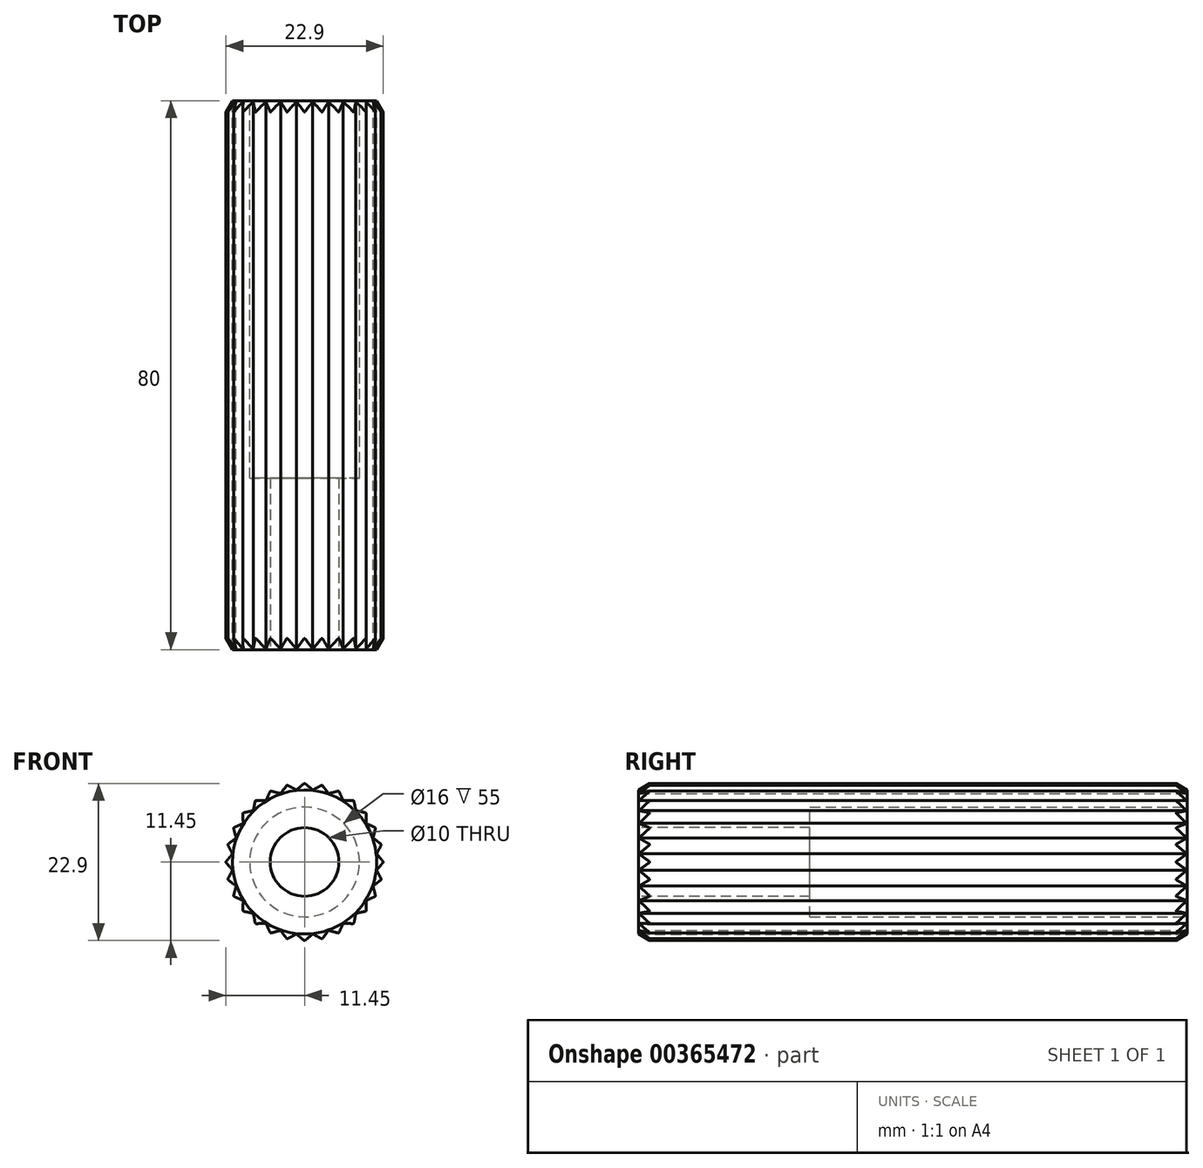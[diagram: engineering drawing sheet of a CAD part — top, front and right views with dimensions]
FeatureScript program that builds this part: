
annotation { "Feature Type Name" : "Feature", "Feature Type Description" : "" }
export const myFeature = defineFeature(function(context is Context, id is Id, definition is map)
    precondition{}
    {
        {
            var Q0;
            Q0=qCreatedBy(makeId("Front.planeOp"),FACE);
            var sketch = newSketch(context, id + "F0", { "sketchPlane" : qUnion([Q0])});
            skCircle(sketch, "E0", {"center": v(0, 0) * mm, "radius": 8 * mm});
            skLineSegment(sketch, "E1", {"start": v(0, 0) * mm, "end": v(0, 8) * mm});
            skLineSegment(sketch, "E2", {"start": v(-0.12, 11.4) * mm, "end": v(-1.73, 10.05) * mm});
            skLineSegment(sketch, "E3.MirrorCS", {"start": v(0.12, 11.4) * mm, "end": v(1.73, 10.05) * mm});
            skPoint(sketch, "E4.visualSharp", {"position": v(0, 11.5) * mm});
            skArc(sketch, "E4.filletArc", {"start": v(0.12, 11.4) * mm, "mid": v(0, 11.45) * mm, "end": v(-0.12, 11.4) * mm});
            skLineSegment(sketch, "E5.1.0", {"start": v(-2.65, 11.1) * mm, "end": v(-3.92, 9.42) * mm});
            skLineSegment(sketch, "E5.1.1", {"start": v(-2.42, 11.14) * mm, "end": v(-0.55, 10.18) * mm});
            skArc(sketch, "E5.1.2", {"start": v(-2.42, 11.14) * mm, "mid": v(-2.55, 11.16) * mm, "end": v(-2.65, 11.1) * mm});
            skLineSegment(sketch, "E5.2.0", {"start": v(-5.05, 10.22) * mm, "end": v(-5.92, 8.3) * mm});
            skLineSegment(sketch, "E5.2.1", {"start": v(-4.84, 10.32) * mm, "end": v(-2.8, 9.8) * mm});
            skArc(sketch, "E5.2.2", {"start": v(-4.84, 10.32) * mm, "mid": v(-4.97, 10.31) * mm, "end": v(-5.05, 10.22) * mm});
            skLineSegment(sketch, "E5.3.0", {"start": v(-7.2, 8.84) * mm, "end": v(-7.62, 6.78) * mm});
            skLineSegment(sketch, "E5.3.1", {"start": v(-7.02, 8.99) * mm, "end": v(-4.92, 8.93) * mm});
            skArc(sketch, "E5.3.2", {"start": v(-7.02, 8.99) * mm, "mid": v(-7.14, 8.95) * mm, "end": v(-7.2, 8.84) * mm});
            skLineSegment(sketch, "E5.4.0", {"start": v(-8.99, 7.02) * mm, "end": v(-8.93, 4.92) * mm});
            skLineSegment(sketch, "E5.4.1", {"start": v(-8.84, 7.2) * mm, "end": v(-6.78, 7.62) * mm});
            skArc(sketch, "E5.4.2", {"start": v(-8.84, 7.2) * mm, "mid": v(-8.95, 7.14) * mm, "end": v(-8.99, 7.02) * mm});
            skLineSegment(sketch, "E5.5.0", {"start": v(-10.32, 4.84) * mm, "end": v(-9.8, 2.8) * mm});
            skLineSegment(sketch, "E5.5.1", {"start": v(-10.22, 5.05) * mm, "end": v(-8.3, 5.92) * mm});
            skArc(sketch, "E5.5.2", {"start": v(-10.22, 5.05) * mm, "mid": v(-10.31, 4.97) * mm, "end": v(-10.32, 4.84) * mm});
            skLineSegment(sketch, "E5.6.0", {"start": v(-11.14, 2.42) * mm, "end": v(-10.18, 0.55) * mm});
            skLineSegment(sketch, "E5.6.1", {"start": v(-11.1, 2.65) * mm, "end": v(-9.42, 3.92) * mm});
            skArc(sketch, "E5.6.2", {"start": v(-11.1, 2.65) * mm, "mid": v(-11.16, 2.55) * mm, "end": v(-11.14, 2.42) * mm});
            skLineSegment(sketch, "E5.7.0", {"start": v(-11.4, -0.12) * mm, "end": v(-10.05, -1.73) * mm});
            skLineSegment(sketch, "E5.7.1", {"start": v(-11.4, 0.12) * mm, "end": v(-10.05, 1.73) * mm});
            skArc(sketch, "E5.7.2", {"start": v(-11.4, 0.12) * mm, "mid": v(-11.45, 0) * mm, "end": v(-11.4, -0.12) * mm});
            skLineSegment(sketch, "E5.8.0", {"start": v(-11.1, -2.65) * mm, "end": v(-9.42, -3.92) * mm});
            skLineSegment(sketch, "E5.8.1", {"start": v(-11.14, -2.42) * mm, "end": v(-10.18, -0.55) * mm});
            skArc(sketch, "E5.8.2", {"start": v(-11.14, -2.42) * mm, "mid": v(-11.16, -2.55) * mm, "end": v(-11.1, -2.65) * mm});
            skLineSegment(sketch, "E5.9.0", {"start": v(-10.22, -5.05) * mm, "end": v(-8.3, -5.92) * mm});
            skLineSegment(sketch, "E5.9.1", {"start": v(-10.32, -4.84) * mm, "end": v(-9.8, -2.8) * mm});
            skArc(sketch, "E5.9.2", {"start": v(-10.32, -4.84) * mm, "mid": v(-10.31, -4.97) * mm, "end": v(-10.22, -5.05) * mm});
            skLineSegment(sketch, "E5.10.0", {"start": v(-8.84, -7.2) * mm, "end": v(-6.78, -7.62) * mm});
            skLineSegment(sketch, "E5.10.1", {"start": v(-8.99, -7.02) * mm, "end": v(-8.93, -4.92) * mm});
            skArc(sketch, "E5.10.2", {"start": v(-8.99, -7.02) * mm, "mid": v(-8.95, -7.14) * mm, "end": v(-8.84, -7.2) * mm});
            skLineSegment(sketch, "E5.11.0", {"start": v(-7.02, -8.99) * mm, "end": v(-4.92, -8.93) * mm});
            skLineSegment(sketch, "E5.11.1", {"start": v(-7.2, -8.84) * mm, "end": v(-7.62, -6.78) * mm});
            skArc(sketch, "E5.11.2", {"start": v(-7.2, -8.84) * mm, "mid": v(-7.14, -8.95) * mm, "end": v(-7.02, -8.99) * mm});
            skLineSegment(sketch, "E5.12.0", {"start": v(-4.84, -10.32) * mm, "end": v(-2.8, -9.8) * mm});
            skLineSegment(sketch, "E5.12.1", {"start": v(-5.05, -10.22) * mm, "end": v(-5.92, -8.3) * mm});
            skArc(sketch, "E5.12.2", {"start": v(-5.05, -10.22) * mm, "mid": v(-4.97, -10.31) * mm, "end": v(-4.84, -10.32) * mm});
            skLineSegment(sketch, "E5.13.0", {"start": v(-2.42, -11.14) * mm, "end": v(-0.55, -10.18) * mm});
            skLineSegment(sketch, "E5.13.1", {"start": v(-2.65, -11.1) * mm, "end": v(-3.92, -9.42) * mm});
            skArc(sketch, "E5.13.2", {"start": v(-2.65, -11.1) * mm, "mid": v(-2.55, -11.16) * mm, "end": v(-2.42, -11.14) * mm});
            skLineSegment(sketch, "E5.14.0", {"start": v(0.12, -11.4) * mm, "end": v(1.73, -10.05) * mm});
            skLineSegment(sketch, "E5.14.1", {"start": v(-0.12, -11.4) * mm, "end": v(-1.73, -10.05) * mm});
            skArc(sketch, "E5.14.2", {"start": v(-0.12, -11.4) * mm, "mid": v(0, -11.45) * mm, "end": v(0.12, -11.4) * mm});
            skLineSegment(sketch, "E5.15.0", {"start": v(2.65, -11.1) * mm, "end": v(3.92, -9.42) * mm});
            skLineSegment(sketch, "E5.15.1", {"start": v(2.42, -11.14) * mm, "end": v(0.55, -10.18) * mm});
            skArc(sketch, "E5.15.2", {"start": v(2.42, -11.14) * mm, "mid": v(2.55, -11.16) * mm, "end": v(2.65, -11.1) * mm});
            skLineSegment(sketch, "E5.16.0", {"start": v(5.05, -10.22) * mm, "end": v(5.92, -8.3) * mm});
            skLineSegment(sketch, "E5.16.1", {"start": v(4.84, -10.32) * mm, "end": v(2.8, -9.8) * mm});
            skArc(sketch, "E5.16.2", {"start": v(4.84, -10.32) * mm, "mid": v(4.97, -10.31) * mm, "end": v(5.05, -10.22) * mm});
            skLineSegment(sketch, "E5.17.0", {"start": v(7.2, -8.84) * mm, "end": v(7.62, -6.78) * mm});
            skLineSegment(sketch, "E5.17.1", {"start": v(7.02, -8.99) * mm, "end": v(4.92, -8.93) * mm});
            skArc(sketch, "E5.17.2", {"start": v(7.02, -8.99) * mm, "mid": v(7.14, -8.95) * mm, "end": v(7.2, -8.84) * mm});
            skLineSegment(sketch, "E5.18.0", {"start": v(8.99, -7.02) * mm, "end": v(8.93, -4.92) * mm});
            skLineSegment(sketch, "E5.18.1", {"start": v(8.84, -7.2) * mm, "end": v(6.78, -7.62) * mm});
            skArc(sketch, "E5.18.2", {"start": v(8.84, -7.2) * mm, "mid": v(8.95, -7.14) * mm, "end": v(8.99, -7.02) * mm});
            skLineSegment(sketch, "E5.19.0", {"start": v(10.32, -4.84) * mm, "end": v(9.8, -2.8) * mm});
            skLineSegment(sketch, "E5.19.1", {"start": v(10.22, -5.05) * mm, "end": v(8.3, -5.92) * mm});
            skArc(sketch, "E5.19.2", {"start": v(10.22, -5.05) * mm, "mid": v(10.31, -4.97) * mm, "end": v(10.32, -4.84) * mm});
            skLineSegment(sketch, "E5.20.0", {"start": v(11.14, -2.42) * mm, "end": v(10.18, -0.55) * mm});
            skLineSegment(sketch, "E5.20.1", {"start": v(11.1, -2.65) * mm, "end": v(9.42, -3.92) * mm});
            skArc(sketch, "E5.20.2", {"start": v(11.1, -2.65) * mm, "mid": v(11.16, -2.55) * mm, "end": v(11.14, -2.42) * mm});
            skLineSegment(sketch, "E5.21.0", {"start": v(11.4, 0.12) * mm, "end": v(10.05, 1.73) * mm});
            skLineSegment(sketch, "E5.21.1", {"start": v(11.4, -0.12) * mm, "end": v(10.05, -1.73) * mm});
            skArc(sketch, "E5.21.2", {"start": v(11.4, -0.12) * mm, "mid": v(11.45, 0) * mm, "end": v(11.4, 0.12) * mm});
            skLineSegment(sketch, "E5.22.0", {"start": v(11.1, 2.65) * mm, "end": v(9.42, 3.92) * mm});
            skLineSegment(sketch, "E5.22.1", {"start": v(11.14, 2.42) * mm, "end": v(10.18, 0.55) * mm});
            skArc(sketch, "E5.22.2", {"start": v(11.14, 2.42) * mm, "mid": v(11.16, 2.55) * mm, "end": v(11.1, 2.65) * mm});
            skLineSegment(sketch, "E5.23.0", {"start": v(10.22, 5.05) * mm, "end": v(8.3, 5.92) * mm});
            skLineSegment(sketch, "E5.23.1", {"start": v(10.32, 4.84) * mm, "end": v(9.8, 2.8) * mm});
            skArc(sketch, "E5.23.2", {"start": v(10.32, 4.84) * mm, "mid": v(10.31, 4.97) * mm, "end": v(10.22, 5.05) * mm});
            skLineSegment(sketch, "E5.24.0", {"start": v(8.84, 7.2) * mm, "end": v(6.78, 7.62) * mm});
            skLineSegment(sketch, "E5.24.1", {"start": v(8.99, 7.02) * mm, "end": v(8.93, 4.92) * mm});
            skArc(sketch, "E5.24.2", {"start": v(8.99, 7.02) * mm, "mid": v(8.95, 7.14) * mm, "end": v(8.84, 7.2) * mm});
            skLineSegment(sketch, "E5.25.0", {"start": v(7.02, 8.99) * mm, "end": v(4.92, 8.93) * mm});
            skLineSegment(sketch, "E5.25.1", {"start": v(7.2, 8.84) * mm, "end": v(7.62, 6.78) * mm});
            skArc(sketch, "E5.25.2", {"start": v(7.2, 8.84) * mm, "mid": v(7.14, 8.95) * mm, "end": v(7.02, 8.99) * mm});
            skLineSegment(sketch, "E5.26.0", {"start": v(4.84, 10.32) * mm, "end": v(2.8, 9.8) * mm});
            skLineSegment(sketch, "E5.26.1", {"start": v(5.05, 10.22) * mm, "end": v(5.92, 8.3) * mm});
            skArc(sketch, "E5.26.2", {"start": v(5.05, 10.22) * mm, "mid": v(4.97, 10.31) * mm, "end": v(4.84, 10.32) * mm});
            skLineSegment(sketch, "E5.27.0", {"start": v(2.42, 11.14) * mm, "end": v(0.55, 10.18) * mm});
            skLineSegment(sketch, "E5.27.1", {"start": v(2.65, 11.1) * mm, "end": v(3.92, 9.42) * mm});
            skArc(sketch, "E5.27.2", {"start": v(2.65, 11.1) * mm, "mid": v(2.55, 11.16) * mm, "end": v(2.42, 11.14) * mm});
            skSolve(sketch);
        }
        {
            var Q0;
            Q0 = qSketchRegion(id + "F0", true);
            extrude(context, id + "F1", {"entities" : qUnion([Q0]), "depth" : 80 * mm});
        }
        {
            var Q0;
            Q0=makeQuery(id+"F1.opExtrude","CAP_FACE",FACE,{"disambiguationData":[OSD([sQuery(id+"F0.wireOp",EDGE,"lSqxqfwO-eqKo-ZCZg-UigB-sFxWdEm8U8hB"),sQuery(id+"F0.wireOp",EDGE,"E0"),sQuery(id+"F0.wireOp",EDGE,"C1UlFKiI-6M3d-ekVj-oFgV-l0cv2vAE1tmQ"),sQuery(id+"F0.wireOp",EDGE,"baf2f13f-041f-44b5-8537-4fbedda5209f0.MirrorCS"),sQuery(id+"F0.wireOp",EDGE,"b2c0e1ce-1615-419f-ab4c-fed52ce990dc.filletArc"),sQuery(id+"F0.wireOp",EDGE,"31b1d020-76b6-4874-875a-db2137b606a0.1.0"),sQuery(id+"F0.wireOp",EDGE,"31b1d020-76b6-4874-875a-db2137b606a0.1.1"),sQuery(id+"F0.wireOp",EDGE,"31b1d020-76b6-4874-875a-db2137b606a0.1.2"),sQuery(id+"F0.wireOp",EDGE,"31b1d020-76b6-4874-875a-db2137b606a0.2.0"),sQuery(id+"F0.wireOp",EDGE,"31b1d020-76b6-4874-875a-db2137b606a0.2.1"),sQuery(id+"F0.wireOp",EDGE,"31b1d020-76b6-4874-875a-db2137b606a0.2.2"),sQuery(id+"F0.wireOp",EDGE,"31b1d020-76b6-4874-875a-db2137b606a0.3.0"),sQuery(id+"F0.wireOp",EDGE,"31b1d020-76b6-4874-875a-db2137b606a0.3.1"),sQuery(id+"F0.wireOp",EDGE,"31b1d020-76b6-4874-875a-db2137b606a0.3.2"),sQuery(id+"F0.wireOp",EDGE,"31b1d020-76b6-4874-875a-db2137b606a0.4.0"),sQuery(id+"F0.wireOp",EDGE,"31b1d020-76b6-4874-875a-db2137b606a0.4.1"),sQuery(id+"F0.wireOp",EDGE,"31b1d020-76b6-4874-875a-db2137b606a0.4.2"),sQuery(id+"F0.wireOp",EDGE,"31b1d020-76b6-4874-875a-db2137b606a0.5.0"),sQuery(id+"F0.wireOp",EDGE,"31b1d020-76b6-4874-875a-db2137b606a0.5.1"),sQuery(id+"F0.wireOp",EDGE,"31b1d020-76b6-4874-875a-db2137b606a0.5.2"),sQuery(id+"F0.wireOp",EDGE,"31b1d020-76b6-4874-875a-db2137b606a0.6.0"),sQuery(id+"F0.wireOp",EDGE,"31b1d020-76b6-4874-875a-db2137b606a0.6.1"),sQuery(id+"F0.wireOp",EDGE,"31b1d020-76b6-4874-875a-db2137b606a0.6.2"),sQuery(id+"F0.wireOp",EDGE,"31b1d020-76b6-4874-875a-db2137b606a0.7.0"),sQuery(id+"F0.wireOp",EDGE,"31b1d020-76b6-4874-875a-db2137b606a0.7.1"),sQuery(id+"F0.wireOp",EDGE,"31b1d020-76b6-4874-875a-db2137b606a0.7.2"),sQuery(id+"F0.wireOp",EDGE,"31b1d020-76b6-4874-875a-db2137b606a0.8.0"),sQuery(id+"F0.wireOp",EDGE,"31b1d020-76b6-4874-875a-db2137b606a0.8.1"),sQuery(id+"F0.wireOp",EDGE,"31b1d020-76b6-4874-875a-db2137b606a0.8.2"),sQuery(id+"F0.wireOp",EDGE,"31b1d020-76b6-4874-875a-db2137b606a0.9.0"),sQuery(id+"F0.wireOp",EDGE,"31b1d020-76b6-4874-875a-db2137b606a0.9.1"),sQuery(id+"F0.wireOp",EDGE,"31b1d020-76b6-4874-875a-db2137b606a0.9.2"),sQuery(id+"F0.wireOp",EDGE,"31b1d020-76b6-4874-875a-db2137b606a0.10.0"),sQuery(id+"F0.wireOp",EDGE,"31b1d020-76b6-4874-875a-db2137b606a0.10.1"),sQuery(id+"F0.wireOp",EDGE,"31b1d020-76b6-4874-875a-db2137b606a0.10.2"),sQuery(id+"F0.wireOp",EDGE,"31b1d020-76b6-4874-875a-db2137b606a0.11.0"),sQuery(id+"F0.wireOp",EDGE,"31b1d020-76b6-4874-875a-db2137b606a0.11.1"),sQuery(id+"F0.wireOp",EDGE,"31b1d020-76b6-4874-875a-db2137b606a0.11.2"),sQuery(id+"F0.wireOp",EDGE,"31b1d020-76b6-4874-875a-db2137b606a0.12.0"),sQuery(id+"F0.wireOp",EDGE,"31b1d020-76b6-4874-875a-db2137b606a0.12.1"),sQuery(id+"F0.wireOp",EDGE,"31b1d020-76b6-4874-875a-db2137b606a0.12.2"),sQuery(id+"F0.wireOp",EDGE,"31b1d020-76b6-4874-875a-db2137b606a0.13.0"),sQuery(id+"F0.wireOp",EDGE,"31b1d020-76b6-4874-875a-db2137b606a0.13.1"),sQuery(id+"F0.wireOp",EDGE,"31b1d020-76b6-4874-875a-db2137b606a0.13.2"),sQuery(id+"F0.wireOp",EDGE,"31b1d020-76b6-4874-875a-db2137b606a0.14.0"),sQuery(id+"F0.wireOp",EDGE,"31b1d020-76b6-4874-875a-db2137b606a0.14.1"),sQuery(id+"F0.wireOp",EDGE,"31b1d020-76b6-4874-875a-db2137b606a0.14.2"),sQuery(id+"F0.wireOp",EDGE,"31b1d020-76b6-4874-875a-db2137b606a0.15.0"),sQuery(id+"F0.wireOp",EDGE,"31b1d020-76b6-4874-875a-db2137b606a0.15.1"),sQuery(id+"F0.wireOp",EDGE,"31b1d020-76b6-4874-875a-db2137b606a0.15.2"),sQuery(id+"F0.wireOp",EDGE,"31b1d020-76b6-4874-875a-db2137b606a0.16.0"),sQuery(id+"F0.wireOp",EDGE,"31b1d020-76b6-4874-875a-db2137b606a0.16.1"),sQuery(id+"F0.wireOp",EDGE,"31b1d020-76b6-4874-875a-db2137b606a0.16.2"),sQuery(id+"F0.wireOp",EDGE,"31b1d020-76b6-4874-875a-db2137b606a0.17.0"),sQuery(id+"F0.wireOp",EDGE,"31b1d020-76b6-4874-875a-db2137b606a0.17.1"),sQuery(id+"F0.wireOp",EDGE,"31b1d020-76b6-4874-875a-db2137b606a0.17.2"),sQuery(id+"F0.wireOp",EDGE,"31b1d020-76b6-4874-875a-db2137b606a0.18.0"),sQuery(id+"F0.wireOp",EDGE,"31b1d020-76b6-4874-875a-db2137b606a0.18.1"),sQuery(id+"F0.wireOp",EDGE,"31b1d020-76b6-4874-875a-db2137b606a0.18.2"),sQuery(id+"F0.wireOp",EDGE,"31b1d020-76b6-4874-875a-db2137b606a0.19.0"),sQuery(id+"F0.wireOp",EDGE,"31b1d020-76b6-4874-875a-db2137b606a0.19.1"),sQuery(id+"F0.wireOp",EDGE,"31b1d020-76b6-4874-875a-db2137b606a0.19.2"),sQuery(id+"F0.wireOp",EDGE,"31b1d020-76b6-4874-875a-db2137b606a0.20.0"),sQuery(id+"F0.wireOp",EDGE,"31b1d020-76b6-4874-875a-db2137b606a0.20.1"),sQuery(id+"F0.wireOp",EDGE,"31b1d020-76b6-4874-875a-db2137b606a0.20.2"),sQuery(id+"F0.wireOp",EDGE,"31b1d020-76b6-4874-875a-db2137b606a0.21.0"),sQuery(id+"F0.wireOp",EDGE,"31b1d020-76b6-4874-875a-db2137b606a0.21.1"),sQuery(id+"F0.wireOp",EDGE,"31b1d020-76b6-4874-875a-db2137b606a0.21.2"),sQuery(id+"F0.wireOp",EDGE,"31b1d020-76b6-4874-875a-db2137b606a0.22.0"),sQuery(id+"F0.wireOp",EDGE,"31b1d020-76b6-4874-875a-db2137b606a0.22.1"),sQuery(id+"F0.wireOp",EDGE,"31b1d020-76b6-4874-875a-db2137b606a0.22.2"),sQuery(id+"F0.wireOp",EDGE,"31b1d020-76b6-4874-875a-db2137b606a0.23.0"),sQuery(id+"F0.wireOp",EDGE,"31b1d020-76b6-4874-875a-db2137b606a0.23.1"),sQuery(id+"F0.wireOp",EDGE,"31b1d020-76b6-4874-875a-db2137b606a0.23.2"),sQuery(id+"F0.wireOp",EDGE,"31b1d020-76b6-4874-875a-db2137b606a0.24.0"),sQuery(id+"F0.wireOp",EDGE,"31b1d020-76b6-4874-875a-db2137b606a0.24.1"),sQuery(id+"F0.wireOp",EDGE,"31b1d020-76b6-4874-875a-db2137b606a0.24.2"),sQuery(id+"F0.wireOp",EDGE,"31b1d020-76b6-4874-875a-db2137b606a0.25.0"),sQuery(id+"F0.wireOp",EDGE,"31b1d020-76b6-4874-875a-db2137b606a0.25.1"),sQuery(id+"F0.wireOp",EDGE,"31b1d020-76b6-4874-875a-db2137b606a0.25.2"),sQuery(id+"F0.wireOp",EDGE,"31b1d020-76b6-4874-875a-db2137b606a0.26.0"),sQuery(id+"F0.wireOp",EDGE,"31b1d020-76b6-4874-875a-db2137b606a0.26.1"),sQuery(id+"F0.wireOp",EDGE,"31b1d020-76b6-4874-875a-db2137b606a0.26.2"),sQuery(id+"F0.wireOp",EDGE,"31b1d020-76b6-4874-875a-db2137b606a0.27.0"),sQuery(id+"F0.wireOp",EDGE,"31b1d020-76b6-4874-875a-db2137b606a0.27.1"),sQuery(id+"F0.wireOp",EDGE,"31b1d020-76b6-4874-875a-db2137b606a0.27.2"),sQuery(id+"F0.wireOp",EDGE,"31b1d020-76b6-4874-875a-db2137b606a0.28.0"),sQuery(id+"F0.wireOp",EDGE,"31b1d020-76b6-4874-875a-db2137b606a0.28.1"),sQuery(id+"F0.wireOp",EDGE,"31b1d020-76b6-4874-875a-db2137b606a0.28.2"),sQuery(id+"F0.wireOp",EDGE,"31b1d020-76b6-4874-875a-db2137b606a0.29.0"),sQuery(id+"F0.wireOp",EDGE,"31b1d020-76b6-4874-875a-db2137b606a0.29.1"),sQuery(id+"F0.wireOp",EDGE,"31b1d020-76b6-4874-875a-db2137b606a0.29.2"),sQuery(id+"F0.wireOp",EDGE,"31b1d020-76b6-4874-875a-db2137b606a0.30.0"),sQuery(id+"F0.wireOp",EDGE,"31b1d020-76b6-4874-875a-db2137b606a0.30.1"),sQuery(id+"F0.wireOp",EDGE,"31b1d020-76b6-4874-875a-db2137b606a0.30.2"),sQuery(id+"F0.wireOp",EDGE,"31b1d020-76b6-4874-875a-db2137b606a0.31.0"),sQuery(id+"F0.wireOp",EDGE,"31b1d020-76b6-4874-875a-db2137b606a0.31.1"),sQuery(id+"F0.wireOp",EDGE,"31b1d020-76b6-4874-875a-db2137b606a0.31.2"),sQuery(id+"F0.wireOp",EDGE,"31b1d020-76b6-4874-875a-db2137b606a0.32.0"),sQuery(id+"F0.wireOp",EDGE,"31b1d020-76b6-4874-875a-db2137b606a0.32.1"),sQuery(id+"F0.wireOp",EDGE,"31b1d020-76b6-4874-875a-db2137b606a0.32.2"),sQuery(id+"F0.wireOp",EDGE,"31b1d020-76b6-4874-875a-db2137b606a0.33.0"),sQuery(id+"F0.wireOp",EDGE,"31b1d020-76b6-4874-875a-db2137b606a0.33.1"),sQuery(id+"F0.wireOp",EDGE,"31b1d020-76b6-4874-875a-db2137b606a0.33.2"),sQuery(id+"F0.wireOp",EDGE,"31b1d020-76b6-4874-875a-db2137b606a0.34.0"),sQuery(id+"F0.wireOp",EDGE,"31b1d020-76b6-4874-875a-db2137b606a0.34.1"),sQuery(id+"F0.wireOp",EDGE,"31b1d020-76b6-4874-875a-db2137b606a0.34.2"),sQuery(id+"F0.wireOp",EDGE,"31b1d020-76b6-4874-875a-db2137b606a0.35.0"),sQuery(id+"F0.wireOp",EDGE,"31b1d020-76b6-4874-875a-db2137b606a0.35.1"),sQuery(id+"F0.wireOp",EDGE,"31b1d020-76b6-4874-875a-db2137b606a0.35.2"),sQuery(id+"F0.wireOp",EDGE,"31b1d020-76b6-4874-875a-db2137b606a0.36.0"),sQuery(id+"F0.wireOp",EDGE,"31b1d020-76b6-4874-875a-db2137b606a0.36.1"),sQuery(id+"F0.wireOp",EDGE,"31b1d020-76b6-4874-875a-db2137b606a0.36.2"),sQuery(id+"F0.wireOp",EDGE,"31b1d020-76b6-4874-875a-db2137b606a0.37.0"),sQuery(id+"F0.wireOp",EDGE,"31b1d020-76b6-4874-875a-db2137b606a0.37.1"),sQuery(id+"F0.wireOp",EDGE,"31b1d020-76b6-4874-875a-db2137b606a0.37.2"),sQuery(id+"F0.wireOp",EDGE,"31b1d020-76b6-4874-875a-db2137b606a0.38.0"),sQuery(id+"F0.wireOp",EDGE,"31b1d020-76b6-4874-875a-db2137b606a0.38.1"),sQuery(id+"F0.wireOp",EDGE,"31b1d020-76b6-4874-875a-db2137b606a0.38.2"),sQuery(id+"F0.wireOp",EDGE,"31b1d020-76b6-4874-875a-db2137b606a0.39.0"),sQuery(id+"F0.wireOp",EDGE,"31b1d020-76b6-4874-875a-db2137b606a0.39.1"),sQuery(id+"F0.wireOp",EDGE,"31b1d020-76b6-4874-875a-db2137b606a0.39.2")])],"isStart":false});
            var sketch = newSketch(context, id + "F2", { "sketchPlane" : qUnion([Q0])});
            skSolve(sketch);
        }
        {
            var Q0;
            Q0=makeQuery(id+"F2.imprint","IMPRINT",FACE,{"disambiguationData":[TD([[makeQuery(id+"F2.imprint","IMPRINT",EDGE,{"derivedFrom":makeQuery(id+"F1.opExtrude","CAP_EDGE",EDGE,{"disambiguationData":[OSD([sQuery(id+"F0.wireOp",EDGE,"E0")])],"isStart":false})}),-1.0]])]});
            var sketch = newSketch(context, id + "F3", { "sketchPlane" : qUnion([Q0])});
            skCircle(sketch, "E6", {"center": v(0, 0) * mm, "radius": 8.97 * mm});
            skCircle(sketch, "E7", {"center": v(0, 0) * mm, "radius": 5 * mm});
            skSolve(sketch);
        }
        {
            var Q0;
            Q0 = qSketchRegion(id + "F3", true);
            extrude(context, id + "F4", {"entities" : qUnion([Q0]), "operationType" : NewBodyOperationType.ADD, "oppositeDirection" : true, "depth" : 25 * mm});
        }
        {
            var Q0;
            Q0=makeQuery(id+"F1.opExtrude","CAP_FACE",FACE,{"disambiguationData":[OSD([sQuery(id+"F0.wireOp",EDGE,"lSqxqfwO-eqKo-ZCZg-UigB-sFxWdEm8U8hB"),sQuery(id+"F0.wireOp",EDGE,"E0"),sQuery(id+"F0.wireOp",EDGE,"C1UlFKiI-6M3d-ekVj-oFgV-l0cv2vAE1tmQ"),sQuery(id+"F0.wireOp",EDGE,"baf2f13f-041f-44b5-8537-4fbedda5209f0.MirrorCS"),sQuery(id+"F0.wireOp",EDGE,"b2c0e1ce-1615-419f-ab4c-fed52ce990dc.filletArc"),sQuery(id+"F0.wireOp",EDGE,"31b1d020-76b6-4874-875a-db2137b606a0.1.0"),sQuery(id+"F0.wireOp",EDGE,"31b1d020-76b6-4874-875a-db2137b606a0.1.1"),sQuery(id+"F0.wireOp",EDGE,"31b1d020-76b6-4874-875a-db2137b606a0.1.2"),sQuery(id+"F0.wireOp",EDGE,"31b1d020-76b6-4874-875a-db2137b606a0.2.0"),sQuery(id+"F0.wireOp",EDGE,"31b1d020-76b6-4874-875a-db2137b606a0.2.1"),sQuery(id+"F0.wireOp",EDGE,"31b1d020-76b6-4874-875a-db2137b606a0.2.2"),sQuery(id+"F0.wireOp",EDGE,"31b1d020-76b6-4874-875a-db2137b606a0.3.0"),sQuery(id+"F0.wireOp",EDGE,"31b1d020-76b6-4874-875a-db2137b606a0.3.1"),sQuery(id+"F0.wireOp",EDGE,"31b1d020-76b6-4874-875a-db2137b606a0.3.2"),sQuery(id+"F0.wireOp",EDGE,"31b1d020-76b6-4874-875a-db2137b606a0.4.0"),sQuery(id+"F0.wireOp",EDGE,"31b1d020-76b6-4874-875a-db2137b606a0.4.1"),sQuery(id+"F0.wireOp",EDGE,"31b1d020-76b6-4874-875a-db2137b606a0.4.2"),sQuery(id+"F0.wireOp",EDGE,"31b1d020-76b6-4874-875a-db2137b606a0.5.0"),sQuery(id+"F0.wireOp",EDGE,"31b1d020-76b6-4874-875a-db2137b606a0.5.1"),sQuery(id+"F0.wireOp",EDGE,"31b1d020-76b6-4874-875a-db2137b606a0.5.2"),sQuery(id+"F0.wireOp",EDGE,"31b1d020-76b6-4874-875a-db2137b606a0.6.0"),sQuery(id+"F0.wireOp",EDGE,"31b1d020-76b6-4874-875a-db2137b606a0.6.1"),sQuery(id+"F0.wireOp",EDGE,"31b1d020-76b6-4874-875a-db2137b606a0.6.2"),sQuery(id+"F0.wireOp",EDGE,"31b1d020-76b6-4874-875a-db2137b606a0.7.0"),sQuery(id+"F0.wireOp",EDGE,"31b1d020-76b6-4874-875a-db2137b606a0.7.1"),sQuery(id+"F0.wireOp",EDGE,"31b1d020-76b6-4874-875a-db2137b606a0.7.2"),sQuery(id+"F0.wireOp",EDGE,"31b1d020-76b6-4874-875a-db2137b606a0.8.0"),sQuery(id+"F0.wireOp",EDGE,"31b1d020-76b6-4874-875a-db2137b606a0.8.1"),sQuery(id+"F0.wireOp",EDGE,"31b1d020-76b6-4874-875a-db2137b606a0.8.2"),sQuery(id+"F0.wireOp",EDGE,"31b1d020-76b6-4874-875a-db2137b606a0.9.0"),sQuery(id+"F0.wireOp",EDGE,"31b1d020-76b6-4874-875a-db2137b606a0.9.1"),sQuery(id+"F0.wireOp",EDGE,"31b1d020-76b6-4874-875a-db2137b606a0.9.2"),sQuery(id+"F0.wireOp",EDGE,"31b1d020-76b6-4874-875a-db2137b606a0.10.0"),sQuery(id+"F0.wireOp",EDGE,"31b1d020-76b6-4874-875a-db2137b606a0.10.1"),sQuery(id+"F0.wireOp",EDGE,"31b1d020-76b6-4874-875a-db2137b606a0.10.2"),sQuery(id+"F0.wireOp",EDGE,"31b1d020-76b6-4874-875a-db2137b606a0.11.0"),sQuery(id+"F0.wireOp",EDGE,"31b1d020-76b6-4874-875a-db2137b606a0.11.1"),sQuery(id+"F0.wireOp",EDGE,"31b1d020-76b6-4874-875a-db2137b606a0.11.2"),sQuery(id+"F0.wireOp",EDGE,"31b1d020-76b6-4874-875a-db2137b606a0.12.0"),sQuery(id+"F0.wireOp",EDGE,"31b1d020-76b6-4874-875a-db2137b606a0.12.1"),sQuery(id+"F0.wireOp",EDGE,"31b1d020-76b6-4874-875a-db2137b606a0.12.2"),sQuery(id+"F0.wireOp",EDGE,"31b1d020-76b6-4874-875a-db2137b606a0.13.0"),sQuery(id+"F0.wireOp",EDGE,"31b1d020-76b6-4874-875a-db2137b606a0.13.1"),sQuery(id+"F0.wireOp",EDGE,"31b1d020-76b6-4874-875a-db2137b606a0.13.2"),sQuery(id+"F0.wireOp",EDGE,"31b1d020-76b6-4874-875a-db2137b606a0.14.0"),sQuery(id+"F0.wireOp",EDGE,"31b1d020-76b6-4874-875a-db2137b606a0.14.1"),sQuery(id+"F0.wireOp",EDGE,"31b1d020-76b6-4874-875a-db2137b606a0.14.2"),sQuery(id+"F0.wireOp",EDGE,"31b1d020-76b6-4874-875a-db2137b606a0.15.0"),sQuery(id+"F0.wireOp",EDGE,"31b1d020-76b6-4874-875a-db2137b606a0.15.1"),sQuery(id+"F0.wireOp",EDGE,"31b1d020-76b6-4874-875a-db2137b606a0.15.2"),sQuery(id+"F0.wireOp",EDGE,"31b1d020-76b6-4874-875a-db2137b606a0.16.0"),sQuery(id+"F0.wireOp",EDGE,"31b1d020-76b6-4874-875a-db2137b606a0.16.1"),sQuery(id+"F0.wireOp",EDGE,"31b1d020-76b6-4874-875a-db2137b606a0.16.2"),sQuery(id+"F0.wireOp",EDGE,"31b1d020-76b6-4874-875a-db2137b606a0.17.0"),sQuery(id+"F0.wireOp",EDGE,"31b1d020-76b6-4874-875a-db2137b606a0.17.1"),sQuery(id+"F0.wireOp",EDGE,"31b1d020-76b6-4874-875a-db2137b606a0.17.2"),sQuery(id+"F0.wireOp",EDGE,"31b1d020-76b6-4874-875a-db2137b606a0.18.0"),sQuery(id+"F0.wireOp",EDGE,"31b1d020-76b6-4874-875a-db2137b606a0.18.1"),sQuery(id+"F0.wireOp",EDGE,"31b1d020-76b6-4874-875a-db2137b606a0.18.2"),sQuery(id+"F0.wireOp",EDGE,"31b1d020-76b6-4874-875a-db2137b606a0.19.0"),sQuery(id+"F0.wireOp",EDGE,"31b1d020-76b6-4874-875a-db2137b606a0.19.1"),sQuery(id+"F0.wireOp",EDGE,"31b1d020-76b6-4874-875a-db2137b606a0.19.2"),sQuery(id+"F0.wireOp",EDGE,"31b1d020-76b6-4874-875a-db2137b606a0.20.0"),sQuery(id+"F0.wireOp",EDGE,"31b1d020-76b6-4874-875a-db2137b606a0.20.1"),sQuery(id+"F0.wireOp",EDGE,"31b1d020-76b6-4874-875a-db2137b606a0.20.2"),sQuery(id+"F0.wireOp",EDGE,"31b1d020-76b6-4874-875a-db2137b606a0.21.0"),sQuery(id+"F0.wireOp",EDGE,"31b1d020-76b6-4874-875a-db2137b606a0.21.1"),sQuery(id+"F0.wireOp",EDGE,"31b1d020-76b6-4874-875a-db2137b606a0.21.2"),sQuery(id+"F0.wireOp",EDGE,"31b1d020-76b6-4874-875a-db2137b606a0.22.0"),sQuery(id+"F0.wireOp",EDGE,"31b1d020-76b6-4874-875a-db2137b606a0.22.1"),sQuery(id+"F0.wireOp",EDGE,"31b1d020-76b6-4874-875a-db2137b606a0.22.2"),sQuery(id+"F0.wireOp",EDGE,"31b1d020-76b6-4874-875a-db2137b606a0.23.0"),sQuery(id+"F0.wireOp",EDGE,"31b1d020-76b6-4874-875a-db2137b606a0.23.1"),sQuery(id+"F0.wireOp",EDGE,"31b1d020-76b6-4874-875a-db2137b606a0.23.2"),sQuery(id+"F0.wireOp",EDGE,"31b1d020-76b6-4874-875a-db2137b606a0.24.0"),sQuery(id+"F0.wireOp",EDGE,"31b1d020-76b6-4874-875a-db2137b606a0.24.1"),sQuery(id+"F0.wireOp",EDGE,"31b1d020-76b6-4874-875a-db2137b606a0.24.2"),sQuery(id+"F0.wireOp",EDGE,"31b1d020-76b6-4874-875a-db2137b606a0.25.0"),sQuery(id+"F0.wireOp",EDGE,"31b1d020-76b6-4874-875a-db2137b606a0.25.1"),sQuery(id+"F0.wireOp",EDGE,"31b1d020-76b6-4874-875a-db2137b606a0.25.2"),sQuery(id+"F0.wireOp",EDGE,"31b1d020-76b6-4874-875a-db2137b606a0.26.0"),sQuery(id+"F0.wireOp",EDGE,"31b1d020-76b6-4874-875a-db2137b606a0.26.1"),sQuery(id+"F0.wireOp",EDGE,"31b1d020-76b6-4874-875a-db2137b606a0.26.2"),sQuery(id+"F0.wireOp",EDGE,"31b1d020-76b6-4874-875a-db2137b606a0.27.0"),sQuery(id+"F0.wireOp",EDGE,"31b1d020-76b6-4874-875a-db2137b606a0.27.1"),sQuery(id+"F0.wireOp",EDGE,"31b1d020-76b6-4874-875a-db2137b606a0.27.2"),sQuery(id+"F0.wireOp",EDGE,"31b1d020-76b6-4874-875a-db2137b606a0.28.0"),sQuery(id+"F0.wireOp",EDGE,"31b1d020-76b6-4874-875a-db2137b606a0.28.1"),sQuery(id+"F0.wireOp",EDGE,"31b1d020-76b6-4874-875a-db2137b606a0.28.2"),sQuery(id+"F0.wireOp",EDGE,"31b1d020-76b6-4874-875a-db2137b606a0.29.0"),sQuery(id+"F0.wireOp",EDGE,"31b1d020-76b6-4874-875a-db2137b606a0.29.1"),sQuery(id+"F0.wireOp",EDGE,"31b1d020-76b6-4874-875a-db2137b606a0.29.2"),sQuery(id+"F0.wireOp",EDGE,"31b1d020-76b6-4874-875a-db2137b606a0.30.0"),sQuery(id+"F0.wireOp",EDGE,"31b1d020-76b6-4874-875a-db2137b606a0.30.1"),sQuery(id+"F0.wireOp",EDGE,"31b1d020-76b6-4874-875a-db2137b606a0.30.2"),sQuery(id+"F0.wireOp",EDGE,"31b1d020-76b6-4874-875a-db2137b606a0.31.0"),sQuery(id+"F0.wireOp",EDGE,"31b1d020-76b6-4874-875a-db2137b606a0.31.1"),sQuery(id+"F0.wireOp",EDGE,"31b1d020-76b6-4874-875a-db2137b606a0.31.2"),sQuery(id+"F0.wireOp",EDGE,"31b1d020-76b6-4874-875a-db2137b606a0.32.0"),sQuery(id+"F0.wireOp",EDGE,"31b1d020-76b6-4874-875a-db2137b606a0.32.1"),sQuery(id+"F0.wireOp",EDGE,"31b1d020-76b6-4874-875a-db2137b606a0.32.2"),sQuery(id+"F0.wireOp",EDGE,"31b1d020-76b6-4874-875a-db2137b606a0.33.0"),sQuery(id+"F0.wireOp",EDGE,"31b1d020-76b6-4874-875a-db2137b606a0.33.1"),sQuery(id+"F0.wireOp",EDGE,"31b1d020-76b6-4874-875a-db2137b606a0.33.2"),sQuery(id+"F0.wireOp",EDGE,"31b1d020-76b6-4874-875a-db2137b606a0.34.0"),sQuery(id+"F0.wireOp",EDGE,"31b1d020-76b6-4874-875a-db2137b606a0.34.1"),sQuery(id+"F0.wireOp",EDGE,"31b1d020-76b6-4874-875a-db2137b606a0.34.2"),sQuery(id+"F0.wireOp",EDGE,"31b1d020-76b6-4874-875a-db2137b606a0.35.0"),sQuery(id+"F0.wireOp",EDGE,"31b1d020-76b6-4874-875a-db2137b606a0.35.1"),sQuery(id+"F0.wireOp",EDGE,"31b1d020-76b6-4874-875a-db2137b606a0.35.2"),sQuery(id+"F0.wireOp",EDGE,"31b1d020-76b6-4874-875a-db2137b606a0.36.0"),sQuery(id+"F0.wireOp",EDGE,"31b1d020-76b6-4874-875a-db2137b606a0.36.1"),sQuery(id+"F0.wireOp",EDGE,"31b1d020-76b6-4874-875a-db2137b606a0.36.2"),sQuery(id+"F0.wireOp",EDGE,"31b1d020-76b6-4874-875a-db2137b606a0.37.0"),sQuery(id+"F0.wireOp",EDGE,"31b1d020-76b6-4874-875a-db2137b606a0.37.1"),sQuery(id+"F0.wireOp",EDGE,"31b1d020-76b6-4874-875a-db2137b606a0.37.2"),sQuery(id+"F0.wireOp",EDGE,"31b1d020-76b6-4874-875a-db2137b606a0.38.0"),sQuery(id+"F0.wireOp",EDGE,"31b1d020-76b6-4874-875a-db2137b606a0.38.1"),sQuery(id+"F0.wireOp",EDGE,"31b1d020-76b6-4874-875a-db2137b606a0.38.2"),sQuery(id+"F0.wireOp",EDGE,"31b1d020-76b6-4874-875a-db2137b606a0.39.0"),sQuery(id+"F0.wireOp",EDGE,"31b1d020-76b6-4874-875a-db2137b606a0.39.1"),sQuery(id+"F0.wireOp",EDGE,"31b1d020-76b6-4874-875a-db2137b606a0.39.2")])],"isStart":true});
            var sketch = newSketch(context, id + "F5", { "sketchPlane" : qUnion([Q0])});
            skCircle(sketch, "E8", {"center": v(0, 0) * mm, "radius": 10.5 * mm});
            skCircle(sketch, "E9", {"center": v(0, 0) * mm, "radius": 13 * mm});
            skSolve(sketch);
        }
        {
            var Q0;
            Q0 = qSketchRegion(id + "F5", true);
            extrude(context, id + "F6", {"entities" : qUnion([Q0]), "operationType" : NewBodyOperationType.REMOVE, "oppositeDirection" : true, "depth" : 3 * mm, "hasDraft" : true, "draftAngle" : 30 * degree, "draftPullDirection" : true});
        }
        {
            var Q0;
            Q0=makeQuery(id+"F2.imprint","IMPRINT",FACE,{"disambiguationData":[TD([[makeQuery(id+"F2.imprint","IMPRINT",EDGE,{"derivedFrom":makeQuery(id+"F1.opExtrude","CAP_EDGE",EDGE,{"disambiguationData":[OSD([sQuery(id+"F0.wireOp",EDGE,"E0")])],"isStart":false})}),-1.0]])]});
            var sketch = newSketch(context, id + "F7", { "sketchPlane" : qUnion([Q0])});
            skCircle(sketch, "E10", {"center": v(0, 0) * mm, "radius": 10.5 * mm});
            skCircle(sketch, "E11", {"center": v(0, 0) * mm, "radius": 13 * mm});
            skSolve(sketch);
        }
        {
            var Q0;
            Q0 = qSketchRegion(id + "F7", true);
            extrude(context, id + "F8", {"entities" : qUnion([Q0]), "operationType" : NewBodyOperationType.REMOVE, "oppositeDirection" : true, "depth" : 3 * mm, "hasDraft" : true, "draftAngle" : 30 * degree, "draftPullDirection" : true});
        }
    });
